# Revit family: Zumtobel RESCLITE PRO TEC-GP
name_source: partatom
category: Lighting Fixtures
revit_build: Autodesk Revit 2018 (Build: 20170223_1515(x64)
units: mm (PartAtom-declared; Revit-internal decimal feet)

## family parameters
Cut with Voids When Loaded = No
Host = Face
Light Source = Yes
OmniClass Number = 23.80.70.11
OmniClass Title = Luminaries for Internal Lighting
Part Type = Normal
Room Calculation Point = No
Round Connector Dimension = Use Diameter
Shared = No

## types (5) — shared parameters
Assembly Code = D5020200
Body = Zumtobel_Metal_White
Color Filter = 16777215
Description = LED Safety luminaire
Dimming Lamp Color Temperature Shift = <None>
Height = 85 mm  [stored 0.278871 ft]
Lamp = LED
Length = 500 mm  [stored 1.64042 ft]
Manufacturer = Zumtobel Lighting
Tilt Angle = 180.00°
URL = http://www.zumtobel.com
Voltage = 230 V
Width = 60 mm  [stored 0.19685 ft]
zero-valued in all types: Default Elevation

## per-type parameters (varying)
| type | Apparent Load | MSC | MSC ESC | Model | Photometric Web File |
| RESCLITE PRO TEC-GP ANT E3D WH | 5 VA | Yes | No | 42185794 | 42185794_(STD_LEO).IES |
| RESCLITE PRO TEC-GP SPOT | 5 VA | Yes | No | 42185796 | 42185796_(STD_LEO).IES |
| RESCLITE PRO TEC-GP ESC90 | 5 VA | No | Yes | 42185795 | 42185795_(STD_LEO).IES |
| RESCLITE PRO TEC-GP ESC HC | 7 VA | Yes | No | 42185824 | 42185824_(STD_LEO).IES |
| RESCLITE PRO TEC-GP ESC | 5 VA | No | Yes | 42185796 | 42185796_(STD_LEO).IES |

note: [stored X ft] marks values corroborated as IEEE doubles in the binary element streams (Revit-internal decimal feet)

## geometry (parser evidence)
native form markers: Sweep x1
no freeform markers — native parametric forms only
